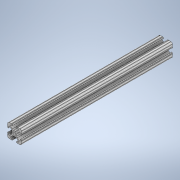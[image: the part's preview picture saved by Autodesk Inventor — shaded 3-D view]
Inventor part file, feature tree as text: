
AUTODESK INVENTOR PART (.ipt)
format: ipt  version: 2020 (Build 240168000, 168)  size: 234,496 bytes
history: native  units: in
note: dims shown in document units (in); Inventor stores cm internally (conversion verified against a paired STEP export)
features: extrude x1, sketch x1
ambient origin geometry x8: Origin, YZ Plane, XZ Plane, XY Plane, X Axis, Y Axis, Z Axis, Center Point
bodies: Solid1 (feature_tree)
feature tree (2):
  extrude  "Extrusion1"  [1 undecoded]
  sketch  "Sketch1"  dims[d0=11.0in d1=0.0in]
note: 1 required parameter value undecoded (feature->parameter linkage not recoverable at this tier; creation-order binding heuristic only, values carry confidence <= 0.55)
